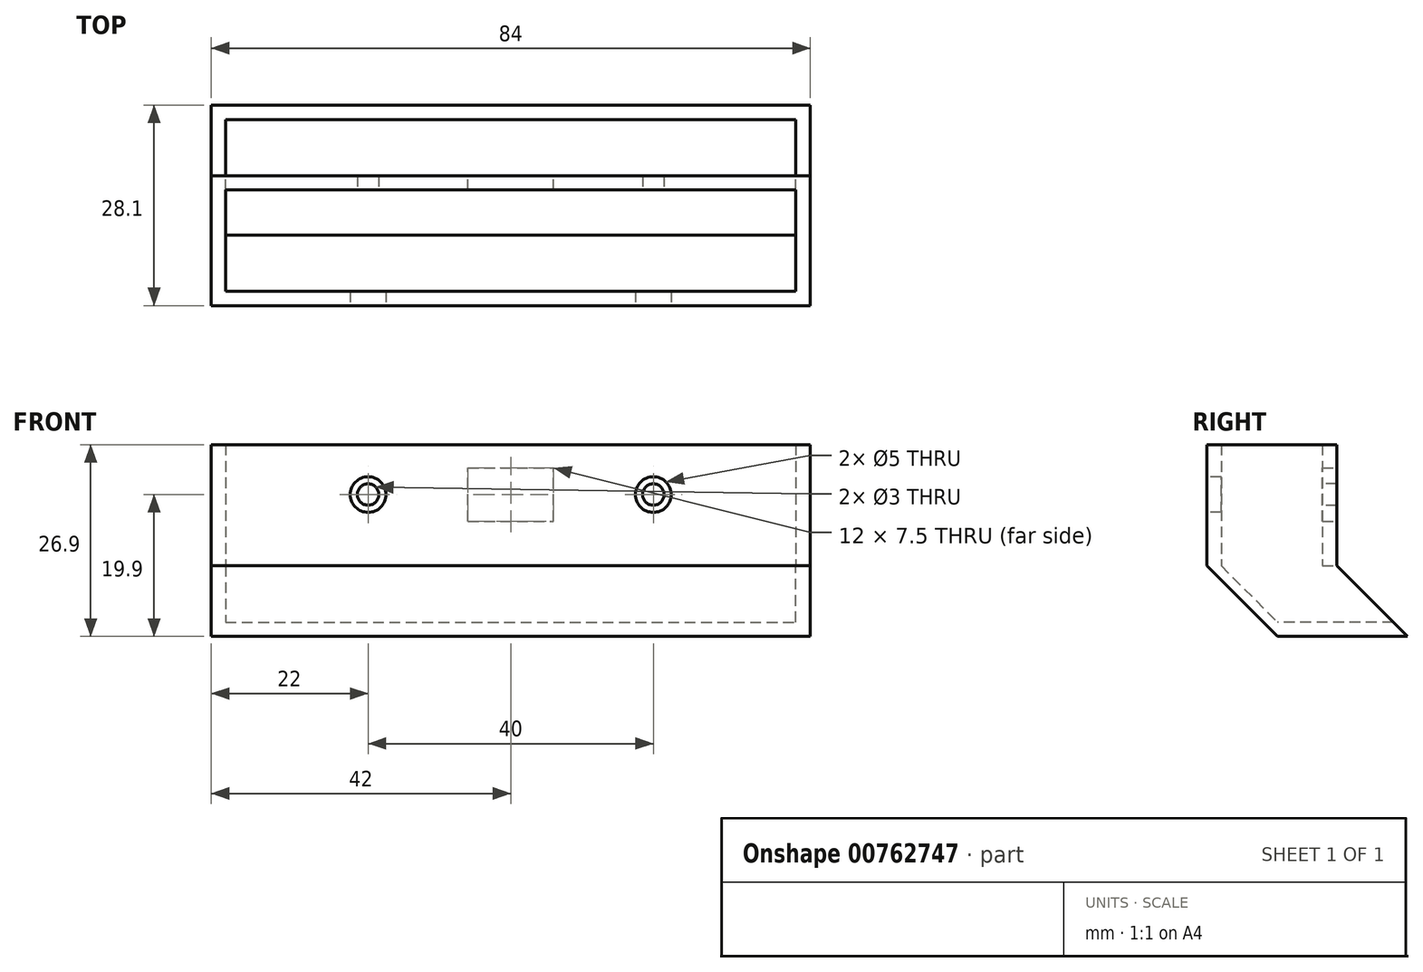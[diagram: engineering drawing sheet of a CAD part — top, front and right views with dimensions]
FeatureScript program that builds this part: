
annotation { "Feature Type Name" : "Feature", "Feature Type Description" : "" }
export const myFeature = defineFeature(function(context is Context, id is Id, definition is map)
    precondition{}
    {
        {
            var Q0;
            Q0=qCreatedBy(makeId("Top.planeOp"),FACE);
            var sketch = newSketch(context, id + "F0", { "sketchPlane" : qUnion([Q0])});
            skLineSegment(sketch, "E0.bottom", {"start": v(40, -7.1) * mm, "end": v(-40, -7.1) * mm});
            skLineSegment(sketch, "E0.top", {"start": v(40, 7.1) * mm, "end": v(-40, 7.1) * mm});
            skLineSegment(sketch, "E0.left", {"start": v(40, -7.1) * mm, "end": v(40, 7.1) * mm});
            skLineSegment(sketch, "E0.right", {"start": v(-40, -7.1) * mm, "end": v(-40, 7.1) * mm});
            skPoint(sketch, "E0.middle", {"position": v(0, 0) * mm});
            skLineSegment(sketch, "E1.0", {"start": v(42, 9.1) * mm, "end": v(-42, 9.1) * mm});
            skLineSegment(sketch, "E1.1", {"start": v(42, -9.1) * mm, "end": v(42, 9.1) * mm});
            skLineSegment(sketch, "E1.2", {"start": v(42, -9.1) * mm, "end": v(-42, -9.1) * mm});
            skLineSegment(sketch, "E1.3", {"start": v(-42, -9.1) * mm, "end": v(-42, 9.1) * mm});
            skSolve(sketch);
        }
        {
            var Q0;
            Q0 = qSketchRegion(id + "F0", true);
            extrude(context, id + "F1", {"entities" : qUnion([Q0]), "depth" : 17 * mm, "offsetDistance" : 25 * mm});
        }
        {
            var Q0;
            Q0=makeQuery(id+"F1.opExtrude","SWEPT_FACE",FACE,{"disambiguationData":[OSD([sQuery(id+"F0.wireOp",EDGE,"E1.2")])]});
            var sketch = newSketch(context, id + "F2", { "sketchPlane" : qUnion([Q0])});
            skLineSegment(sketch, "E2", {"start": v(42, 10) * mm, "end": v(-42, 10) * mm, "construction": true});
            skPoint(sketch, "E3", {"position": v(-20, 10) * mm});
            skPoint(sketch, "E4.MirrorP", {"position": v(20, 10) * mm});
            skPoint(sketch, "E5.middle", {"position": v(0, 10) * mm});
            skSolve(sketch);
        }
        {
            var Q0;
            Q0=sQuery(id+"F2.wireOp",VERTEX,"E3");
            var Q1;
            Q1=sQuery(id+"F2.wireOp",VERTEX,"E4.MirrorP");
            var Q2;
            Q2=makeQuery(id+"F1.opExtrude","SWEPT_BODY",BODY,{"disambiguationData":[OSD([sQuery(id+"F0.wireOp",EDGE,"E0.bottom"),sQuery(id+"F0.wireOp",EDGE,"E0.top"),sQuery(id+"F0.wireOp",EDGE,"E0.left"),sQuery(id+"F0.wireOp",EDGE,"E0.right"),sQuery(id+"F0.wireOp",EDGE,"E1.0"),sQuery(id+"F0.wireOp",EDGE,"E1.1"),sQuery(id+"F0.wireOp",EDGE,"E1.2"),sQuery(id+"F0.wireOp",EDGE,"E1.3")])]});
            hole(context, id + "F3", {"style" : HoleStyle.C_BORE, "endStyle" : HoleEndStyle.THROUGH, "holeDiameter" : 3 * mm, "cBoreDiameter" : 5 * mm, "cBoreDepth" : 5 * mm, "majorDiameter" : 5 * mm, "isTappedThrough" : true, "tappedDepth" : 12 * mm, "tapClearance" : 3, "locations" : qUnion([Q0, Q1]), "scope" : qUnion([Q2])});
        }
        {
            var Q0;
            Q0=makeQuery(id+"F1.opExtrude","SWEPT_FACE",FACE,{"disambiguationData":[OSD([sQuery(id+"F0.wireOp",EDGE,"E1.0")])]});
            var sketch = newSketch(context, id + "F4", { "sketchPlane" : qUnion([Q0])});
            skLineSegment(sketch, "E6", {"start": v(-20, 10) * mm, "end": v(20, 10) * mm, "construction": true});
            skLineSegment(sketch, "E7.bottom", {"start": v(6, 6.25) * mm, "end": v(-6, 6.25) * mm});
            skLineSegment(sketch, "E7.top", {"start": v(6, 13.75) * mm, "end": v(-6, 13.75) * mm});
            skLineSegment(sketch, "E7.left", {"start": v(6, 6.25) * mm, "end": v(6, 13.75) * mm});
            skLineSegment(sketch, "E7.right", {"start": v(-6, 6.25) * mm, "end": v(-6, 13.75) * mm});
            skPoint(sketch, "E7.middle", {"position": v(0, 10) * mm});
            skSolve(sketch);
        }
        {
            var Q0;
            Q0=makeQuery(id+"F4.imprint","IMPRINT",FACE,{"disambiguationData":[TD([[makeQuery(id+"F4.imprint","IMPRINT",EDGE,{"derivedFrom":sQuery(id+"F4.wireOp",EDGE,"E7.bottom")}),-1.0]])]});
            extrude(context, id + "F5", {"entities" : qUnion([Q0]), "operationType" : NewBodyOperationType.REMOVE, "oppositeDirection" : true, "depth" : 2 * mm, "offsetDistance" : 25 * mm});
        }
        {
            var Q0;
            Q0=makeQuery(id+"F1.opExtrude","SWEPT_FACE",FACE,{"disambiguationData":[OSD([sQuery(id+"F0.wireOp",EDGE,"E1.3")])]});
            var sketch = newSketch(context, id + "F6", { "sketchPlane" : qUnion([Q0])});
            skLineSegment(sketch, "E8", {"start": v(-9.1, 0) * mm, "end": v(-19, -9.9) * mm});
            skLineSegment(sketch, "E9", {"start": v(9.1, 0) * mm, "end": v(-0.8, -9.9) * mm});
            skLineSegment(sketch, "E10", {"start": v(-19, -9.9) * mm, "end": v(-0.8, -9.9) * mm});
            skLineSegment(sketch, "E11", {"start": v(-19, -9.9) * mm, "end": v(-9.1, 0) * mm});
            skSolve(sketch);
        }
        {
            var Q0;
            Q0=makeQuery(id+"F6.imprint","IMPRINT",FACE,{"disambiguationData":[TD([[makeQuery(id+"F6.imprint","IMPRINT",EDGE,{"derivedFrom":sQuery(id+"F6.wireOp",EDGE,"E10")}),1.0]])]});
            extrude(context, id + "F7", {"entities" : qUnion([Q0]), "operationType" : NewBodyOperationType.ADD, "oppositeDirection" : true, "depth" : 2 * mm, "offsetDistance" : 25 * mm});
        }
        {
            var Q0;
            Q0=makeQuery(id+"F1.opExtrude","SWEPT_FACE",FACE,{"disambiguationData":[OSD([sQuery(id+"F0.wireOp",EDGE,"E1.1")])]});
            var sketch = newSketch(context, id + "F8", { "sketchPlane" : qUnion([Q0])});
            skLineSegment(sketch, "E12", {"start": v(-9.1, 0) * mm, "end": v(0.8, -9.9) * mm});
            skLineSegment(sketch, "E13", {"start": v(0.8, -9.9) * mm, "end": v(19, -9.9) * mm});
            skLineSegment(sketch, "E14", {"start": v(19, -9.9) * mm, "end": v(9.1, 0) * mm});
            skSolve(sketch);
        }
        {
            var Q0;
            Q0=makeQuery(id+"F8.imprint","IMPRINT",FACE,{"disambiguationData":[TD([[makeQuery(id+"F8.imprint","IMPRINT",EDGE,{"derivedFrom":sQuery(id+"F8.wireOp",EDGE,"E12")}),1.0]])]});
            extrude(context, id + "F9", {"entities" : qUnion([Q0]), "operationType" : NewBodyOperationType.ADD, "oppositeDirection" : true, "depth" : 2 * mm, "offsetDistance" : 25 * mm});
        }
        {
            var Q0;
            Q0=makeQuery(id+"F9.boolean.opBoolean","MERGE",FACE,{"derivedFrom":[makeQuery(id+"F1.opExtrude","SWEPT_FACE",FACE,{"disambiguationData":[OSD([sQuery(id+"F0.wireOp",EDGE,"E0.left")])]}),makeQuery(id+"F9.opExtrude","CAP_FACE",FACE,{"disambiguationData":[OSD([sQuery(id+"F0.wireOp",EDGE,"E1.1"),sQuery(id+"F8.wireOp",EDGE,"E12"),sQuery(id+"F8.wireOp",EDGE,"E13"),sQuery(id+"F8.wireOp",EDGE,"E14")])],"isStart":false})]});
            var sketch = newSketch(context, id + "F10", { "sketchPlane" : qUnion([Q0])});
            skLineSegment(sketch, "E15", {"start": v(7.1, 0) * mm, "end": v(-2.8, -9.9) * mm});
            skSolve(sketch);
        }
        {
            var Q0;
            Q0 = qSketchRegion(id + "F10", true);
            var Q1;
            {var subQ0=sQuery(id+"F10.wireOp",EDGE,"E15");Q1=makeQuery(id+"F10.imprint","IMPRINT",FACE,{"disambiguationData":[TD([[makeQuery(id+"F10.imprint","IMPRINT",EDGE,{"derivedFrom":subQ0}),1.0]])]});}
            extrude(context, id + "F11", {"entities" : qUnion([Q0, Q1]), "operationType" : NewBodyOperationType.ADD, "depth" : 80 * mm, "offsetDistance" : 25 * mm});
        }
        {
            var Q0;
            Q0=makeQuery(id+"F9.boolean.opBoolean","MERGE",FACE,{"derivedFrom":[makeQuery(id+"F1.opExtrude","SWEPT_FACE",FACE,{"disambiguationData":[OSD([sQuery(id+"F0.wireOp",EDGE,"E0.left")])]}),makeQuery(id+"F9.opExtrude","CAP_FACE",FACE,{"disambiguationData":[OSD([sQuery(id+"F0.wireOp",EDGE,"E1.1"),sQuery(id+"F8.wireOp",EDGE,"E12"),sQuery(id+"F8.wireOp",EDGE,"E13"),sQuery(id+"F8.wireOp",EDGE,"E14")])],"isStart":false})]});
            var sketch = newSketch(context, id + "F12", { "sketchPlane" : qUnion([Q0])});
            skLineSegment(sketch, "E16", {"start": v(-17, -7.9) * mm, "end": v(-0.8, -7.9) * mm});
            skSolve(sketch);
        }
        {
            var Q0;
            {var subQ0=sQuery(id+"F12.wireOp",EDGE,"E16");Q0=makeQuery(id+"F12.imprint","IMPRINT",FACE,{"disambiguationData":[TD([[makeQuery(id+"F12.imprint","IMPRINT",EDGE,{"derivedFrom":subQ0}),-1.0]])]});}
            extrude(context, id + "F13", {"entities" : qUnion([Q0]), "operationType" : NewBodyOperationType.ADD, "depth" : 80 * mm, "offsetDistance" : 25 * mm});
        }
    });
